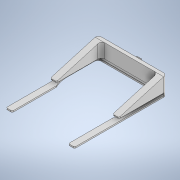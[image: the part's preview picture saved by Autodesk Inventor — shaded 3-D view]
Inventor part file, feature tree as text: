
AUTODESK INVENTOR PART (.ipt)
format: ipt  version: 2020 (Build 240168000, 168)  size: 255,488 bytes
history: native  units: in
note: dims shown in document units (in); Inventor stores cm internally (conversion verified against a paired STEP export)
features: sketch x11, extrude x9, fillet x5
ambient origin geometry x8: Origin, YZ Plane, XZ Plane, XY Plane, X Axis, Y Axis, Z Axis, Center Point
bodies: Solid1 (feature_tree)
feature tree (25):
  extrude  "Extrusion1"  Depth=3.937in
  extrude  "Extrusion2"  TaperAngle=0.0deg  [1 undecoded]
  extrude  "Extrusion7"  Depth=3.622in
  extrude  "Extrusion8"  Depth=0.2126in TaperAngle=0.0deg
  extrude  "Extrusion9"  Depth=3.5827in TaperAngle=0.0deg
  extrude  "Extrusion10"  Depth=0.1969in
  fillet  "Fillet1"  Radius=0.1969in
  fillet  "Fillet2"  Radius=0.3307in
  extrude  "Extrusion11"  Depth=0.3937in TaperAngle=0.0deg
  extrude  "Extrusion12"  Depth=0.2126in
  fillet  "Fillet5"  Radius=0.1654in
  sketch  "Sketch18"  dims[d45=0.0in d46=0.0in d47=0.0787in d48=4.5485in d49=0.1339in]
  sketch  "Sketch19"  dims[d50=0.0787in]
  extrude  "Extrusion13"  Depth=0.0787in
  fillet  "Fillet7"  Radius=4.5485in
  fillet  "Fillet8"  Radius=0.1339in
  sketch  "Sketch1"  dims[d0=3.937in d1=4.7244in]
  sketch  "Sketch2"  dims[d2=1.0236in d3=0.0in d9=0.0in d10=0.0in]
  sketch  "Sketch11"  dims[d23=4.5276in d24=3.622in]
  sketch  "Sketch13"  dims[d25=1.752in d26=0.2126in d27=0.0in]
  sketch  "Sketch14"  dims[d28=3.5827in d29=0.0in d30=3.5827in d31=0.0in]
  sketch  "Sketch15"  dims[d32=1.9685in d33=0.0in d34=0.1969in d35=0.1969in d38=0.3307in]
  sketch  "Sketch16"  dims[d39=0.1181in d40=0.3937in d41=0.0in]
  sketch  "Sketch17"  dims[d42=0.2126in d43=0.1654in d44=0.1654in]
  sketch  "Sketch20"  dims[d51=0.811in d52=1.9544in d53=2.5731in d54=0.748in d56=0.5906in d57=0.0in d58=0.0787in d59=0.0787in d4=0.0197in d5=0.0344in]
note: 1 required parameter value undecoded (feature->parameter linkage not recoverable at this tier; creation-order binding heuristic only, values carry confidence <= 0.55)
